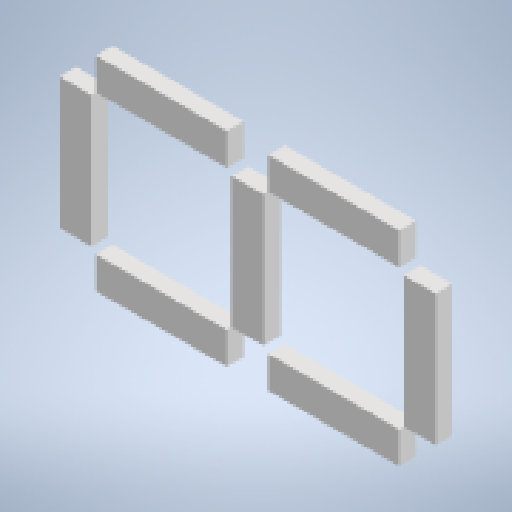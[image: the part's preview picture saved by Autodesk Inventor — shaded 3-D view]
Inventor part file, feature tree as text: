
AUTODESK INVENTOR PART (.ipt)
format: ipt  version: 2024.2 (Build 282272000, 272)  size: 166,400 bytes
history: native  units: mm
features: extrude x1, sketch x1
ambient origin geometry x8: Origin, YZ Plane, XZ Plane, XY Plane, X Axis, Y Axis, Z Axis, Center Point
bodies: Solid1 (feature_tree)
feature tree (2):
  extrude  "Extrusion1"  Depth=92.0mm
  sketch  "Sketch1"  dims[d1=100.0mm d2=92.0mm d3=92.0mm d4=17.0mm d5=17.0mm d6=70.0mm d7=70.0mm d8=92.0mm d9=9.0mm d10=0.0mm]
